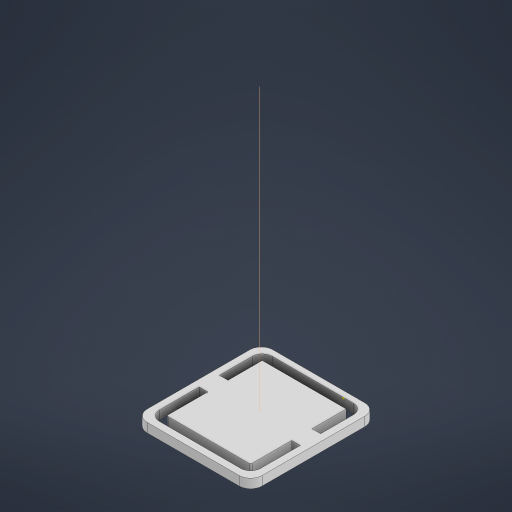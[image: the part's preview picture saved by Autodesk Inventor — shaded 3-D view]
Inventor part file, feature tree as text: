
AUTODESK INVENTOR PART (.ipt)
format: ipt  version: 2024.1 (Build 281209000, 209)  size: 1,451,008 bytes
history: native  units: mm
features: other x3, extrude x1, boolean_combine x1, sketch x1, projected_geometry x1
ambient origin geometry x8: Origin, YZ Plane, XZ Plane, XY Plane, X Axis, Y Axis, Z Axis, Center Point
bodies: Solid3 (feature_tree)
feature tree (7):
  other  "CloakTop.ipt"
  extrude  "Extrusion1"  Depth=3.0mm
  boolean_combine  "Combine1"
  other  "Solid2::CloakTop.ipt"
  other  "TaggingFeature1"
  sketch  "Sketch2"  dims[d0=10.0mm d1=3.0mm d2=0.4mm d3=0.4mm d4=3.0mm d5=3.0mm d6=3.0mm d7=5.0mm d8=4.0mm d9=0.0mm]
  projected_geometry  "Project Cut Edges1"
